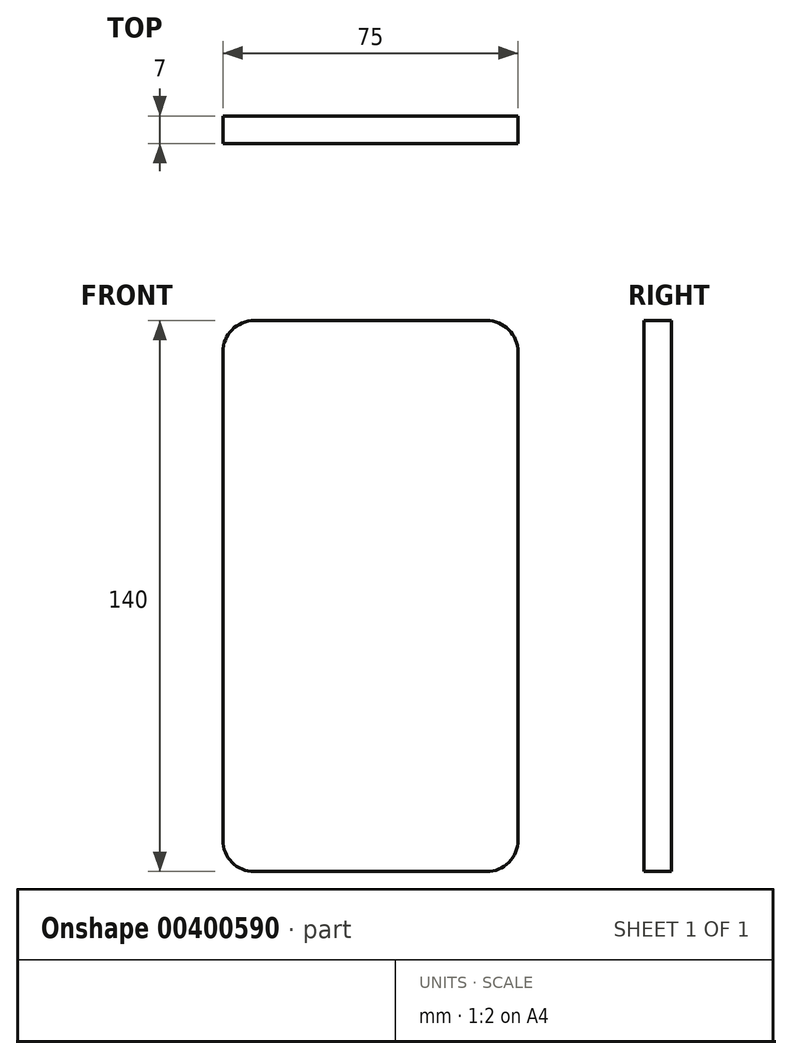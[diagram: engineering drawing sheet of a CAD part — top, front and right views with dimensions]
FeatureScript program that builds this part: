
annotation { "Feature Type Name" : "Feature", "Feature Type Description" : "" }
export const myFeature = defineFeature(function(context is Context, id is Id, definition is map)
    precondition{}
    {
        {
            var Q0;
            Q0=qCreatedBy(makeId("Front.planeOp"),FACE);
            var sketch = newSketch(context, id + "F0", { "sketchPlane" : qUnion([Q0])});
            skLineSegment(sketch, "E0.bottom", {"start": v(37.5, 70) * mm, "end": v(-37.5, 70) * mm});
            skLineSegment(sketch, "E0.top", {"start": v(37.5, -70) * mm, "end": v(-37.5, -70) * mm});
            skLineSegment(sketch, "E0.left", {"start": v(37.5, 70) * mm, "end": v(37.5, -70) * mm});
            skLineSegment(sketch, "E0.right", {"start": v(-37.5, 70) * mm, "end": v(-37.5, -70) * mm});
            skPoint(sketch, "E0.middle", {"position": v(0, 0) * mm});
            skSolve(sketch);
        }
        {
            var Q0;
            Q0 = qSketchRegion(id + "F0", true);
            extrude(context, id + "F1", {"entities" : qUnion([Q0]), "endBound" : BoundingType.SYMMETRIC, "depth" : 7 * mm});
        }
        {
            var Q0;
            Q0=makeQuery(id+"F1.opExtrude","SWEPT_EDGE",EDGE,{"disambiguationData":[OSD([sQuery(id+"F0.wireOp",EDGE,"E0.bottom"),sQuery(id+"F0.wireOp",EDGE,"E0.right")])]});
            var Q1;
            Q1=makeQuery(id+"F1.opExtrude","SWEPT_EDGE",EDGE,{"disambiguationData":[OSD([sQuery(id+"F0.wireOp",EDGE,"E0.bottom"),sQuery(id+"F0.wireOp",EDGE,"E0.left")])]});
            var Q2;
            Q2=makeQuery(id+"F1.opExtrude","SWEPT_EDGE",EDGE,{"disambiguationData":[OSD([sQuery(id+"F0.wireOp",EDGE,"E0.top"),sQuery(id+"F0.wireOp",EDGE,"E0.left")])]});
            var Q3;
            Q3=makeQuery(id+"F1.opExtrude","SWEPT_EDGE",EDGE,{"disambiguationData":[OSD([sQuery(id+"F0.wireOp",EDGE,"E0.top"),sQuery(id+"F0.wireOp",EDGE,"E0.right")])]});
            fillet(context, id + "F2", {"entities" : qUnion([Q0, Q1, Q2, Q3]), "radius" : 8 * mm, "tangentPropagation" : true, "allowEdgeOverflow" : false});
        }
    });
